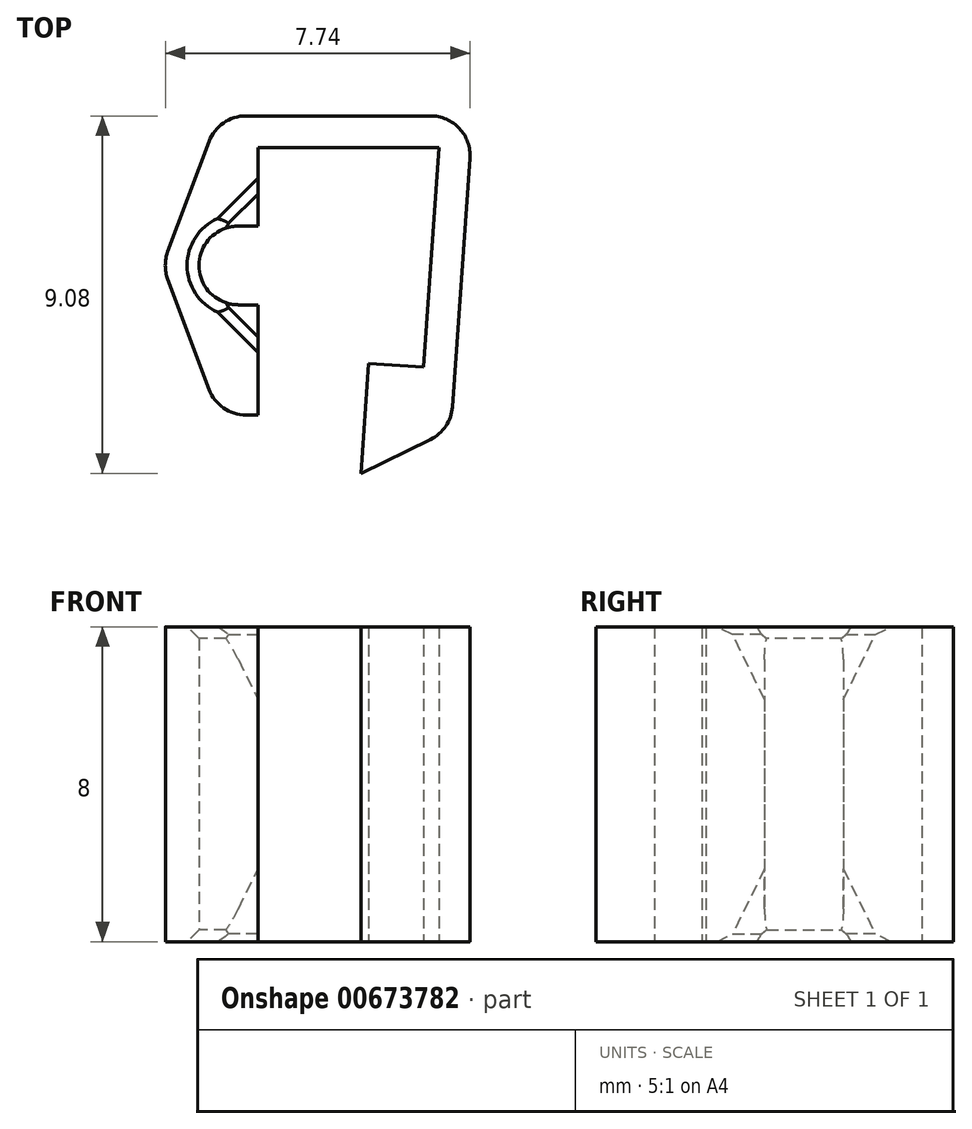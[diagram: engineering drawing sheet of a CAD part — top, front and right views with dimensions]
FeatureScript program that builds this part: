
annotation { "Feature Type Name" : "Feature", "Feature Type Description" : "" }
export const myFeature = defineFeature(function(context is Context, id is Id, definition is map)
    precondition{}
    {
        {
            var Q0;
            Q0=qCreatedBy(makeId("Top.planeOp"),FACE);
            var sketch = newSketch(context, id + "F0", { "sketchPlane" : qUnion([Q0])});
            skLineSegment(sketch, "E0", {"start": v(0, 0) * mm, "end": v(-0.4, -5.59) * mm});
            skLineSegment(sketch, "E1", {"start": v(-0.4, -5.59) * mm, "end": v(-1.79, -5.49) * mm});
            skLineSegment(sketch, "E2", {"start": v(-1.79, -5.49) * mm, "end": v(-1.98, -8.28) * mm});
            skLineSegment(sketch, "E3", {"start": v(-1.98, -8.28) * mm, "end": v(0.3, -7.17) * mm});
            skLineSegment(sketch, "E4", {"start": v(0.3, -7.17) * mm, "end": v(0.86, 0.8) * mm});
            skLineSegment(sketch, "E5", {"start": v(0.86, 0.8) * mm, "end": v(-5.6, 0.8) * mm});
            skLineSegment(sketch, "E6", {"start": v(-5.1, -4) * mm, "end": v(-4.6, -4) * mm});
            skLineSegment(sketch, "E7", {"start": v(-4.6, -4) * mm, "end": v(-4.6, -6.8) * mm});
            skLineSegment(sketch, "E8", {"start": v(-7.02, -3) * mm, "end": v(-5.6, -6.8) * mm});
            skLineSegment(sketch, "E9", {"start": v(-5.6, -6.8) * mm, "end": v(-4.6, -6.8) * mm});
            skLineSegment(sketch, "E10", {"start": v(-4.6, -2) * mm, "end": v(-5.1, -2) * mm});
            skLineSegment(sketch, "E11", {"start": v(0, 0) * mm, "end": v(-4.6, 0) * mm});
            skLineSegment(sketch, "E12", {"start": v(-4.6, 0) * mm, "end": v(-4.6, -2) * mm});
            skArc(sketch, "E13", {"start": v(-5.1, -2) * mm, "mid": v(-6.1, -3) * mm, "end": v(-5.1, -4) * mm});
            skLineSegment(sketch, "E14", {"start": v(-7.02, -3) * mm, "end": v(-5.6, 0.8) * mm});
            skLineSegment(sketch, "E15", {"start": v(-5.6, -6.8) * mm, "end": v(-5.6, 0.8) * mm, "construction": true});
            skLineSegment(sketch, "E16", {"start": v(-5.1, -3) * mm, "end": v(-6.04, -2.65) * mm, "construction": true});
            skLineSegment(sketch, "E17", {"start": v(-6.04, -2.65) * mm, "end": v(-6.79, -2.37) * mm, "construction": true});
            skLineSegment(sketch, "E18", {"start": v(0, 0) * mm, "end": v(0, 0.8) * mm, "construction": true});
            skLineSegment(sketch, "E19", {"start": v(0.8, -0.06) * mm, "end": v(0, 0) * mm, "construction": true});
            skSolve(sketch);
        }
        {
            var Q0;
            Q0=qSketchRegion(id+"F0",true);
            extrude(context, id + "F1", {"entities" : qUnion([Q0]), "depth" : 4 * mm, "offsetDistance" : 25 * mm});
        }
        {
            var Q0;
            Q0=makeQuery(id+"F1.opExtrude","CAP_FACE",FACE,{"disambiguationData":[OSD([sQuery(id+"F0.wireOp",EDGE,"E0"),sQuery(id+"F0.wireOp",EDGE,"E1"),sQuery(id+"F0.wireOp",EDGE,"E2"),sQuery(id+"F0.wireOp",EDGE,"E3"),sQuery(id+"F0.wireOp",EDGE,"E4"),sQuery(id+"F0.wireOp",EDGE,"E5"),sQuery(id+"F0.wireOp",EDGE,"3qQk4eZ2-qFBK-7vCE-47k8-9gwiF50xY8QG"),sQuery(id+"F0.wireOp",EDGE,"FwfflrWr-MbD4-lGZ7-AJjG-6BkzjliF19me"),sQuery(id+"F0.wireOp",EDGE,"E6"),sQuery(id+"F0.wireOp",EDGE,"E7"),sQuery(id+"F0.wireOp",EDGE,"dEJFUDGW-VdPt-nXIw-TINV-OlQtnsbTHH9Y"),sQuery(id+"F0.wireOp",EDGE,"E8"),sQuery(id+"F0.wireOp",EDGE,"E9")])],"isStart":false});
            var sketch = newSketch(context, id + "F2", { "sketchPlane" : qUnion([Q0])});
            skLineSegment(sketch, "E20", {"start": v(-5.8, -3.7) * mm, "end": v(-4.6, -4.91) * mm});
            skLineSegment(sketch, "E21", {"start": v(-4.6, -4.91) * mm, "end": v(-4.6, -4) * mm});
            skLineSegment(sketch, "E22", {"start": v(-4.6, -4) * mm, "end": v(-5.8, -3.7) * mm});
            skLineSegment(sketch, "E23", {"start": v(-5.8, -2.3) * mm, "end": v(-4.6, -1.09) * mm});
            skLineSegment(sketch, "E24", {"start": v(-4.6, -1.09) * mm, "end": v(-4.6, -2) * mm});
            skLineSegment(sketch, "E25", {"start": v(-4.6, -2) * mm, "end": v(-5.8, -2.3) * mm});
            skSolve(sketch);
        }
        {
            var Q0;
            Q0=qSketchRegion(id+"F2",true);
            extrude(context, id + "F3", {"entities" : qUnion([Q0]), "operationType" : NewBodyOperationType.REMOVE, "oppositeDirection" : true, "depth" : 2 * mm});
        }
        {
            var Q0;
            Q0=makeQuery(id+"F3.boolean.opBoolean","COPY",EDGE,{"derivedFrom":makeQuery(id+"F3.opExtrude","CAP_EDGE",EDGE,{"disambiguationData":[OSD([sQuery(id+"F2.wireOp",EDGE,"E20")])],"isStart":false})});
            chamfer(context, id + "F4", {"entities" : qUnion([Q0]), "chamferType" : ChamferType.TWO_OFFSETS, "width1" : .7 * mm, "oppositeDirection" : false, "width2" : 2 * mm, "tangentPropagation" : true});
        }
        {
            var Q0;
            Q0=makeQuery(id+"F3.boolean.opBoolean","COPY",EDGE,{"derivedFrom":makeQuery(id+"F3.opExtrude","CAP_EDGE",EDGE,{"disambiguationData":[OSD([sQuery(id+"F2.wireOp",EDGE,"E23")])],"isStart":false})});
            chamfer(context, id + "F5", {"entities" : qUnion([Q0]), "chamferType" : ChamferType.TWO_OFFSETS, "width1" : 2 * mm, "oppositeDirection" : false, "width2" : .7 * mm, "tangentPropagation" : true});
        }
        {
            var Q0;
            Q0=makeQuery(id+"F1.opExtrude","SWEPT_EDGE",EDGE,{"disambiguationData":[OSD([sQuery(id+"F0.wireOp",EDGE,"E4"),sQuery(id+"F0.wireOp",EDGE,"E5")])]});
            var Q1;
            Q1=makeQuery(id+"F1.opExtrude","SWEPT_EDGE",EDGE,{"disambiguationData":[OSD([sQuery(id+"F0.wireOp",EDGE,"E3"),sQuery(id+"F0.wireOp",EDGE,"E4")])]});
            var Q2;
            Q2=makeQuery(id+"F1.opExtrude","SWEPT_EDGE",EDGE,{"disambiguationData":[OSD([sQuery(id+"F0.wireOp",EDGE,"E8"),sQuery(id+"F0.wireOp",EDGE,"E9")])]});
            var Q3;
            Q3=makeQuery(id+"F1.opExtrude","SWEPT_EDGE",EDGE,{"disambiguationData":[OSD([sQuery(id+"F0.wireOp",EDGE,"E8"),sQuery(id+"F0.wireOp",EDGE,"E14")])]});
            var Q4;
            Q4=makeQuery(id+"F1.opExtrude","SWEPT_EDGE",EDGE,{"disambiguationData":[OSD([sQuery(id+"F0.wireOp",EDGE,"E5"),sQuery(id+"F0.wireOp",EDGE,"E14")])]});
            fillet(context, id + "F6", {"entities" : qUnion([Q0, Q1, Q2, Q3, Q4]), "radius" : 1 * mm, "tangentPropagation" : true, "allowEdgeOverflow" : false});
        }
        {
            var Q0;
            Q0=makeQuery(id+"F1.opExtrude","SWEPT_BODY",BODY,{"disambiguationData":[OSD([sQuery(id+"F0.wireOp",EDGE,"E0"),sQuery(id+"F0.wireOp",EDGE,"E1"),sQuery(id+"F0.wireOp",EDGE,"E2"),sQuery(id+"F0.wireOp",EDGE,"E3"),sQuery(id+"F0.wireOp",EDGE,"E4"),sQuery(id+"F0.wireOp",EDGE,"E5"),sQuery(id+"F0.wireOp",EDGE,"3qQk4eZ2-qFBK-7vCE-47k8-9gwiF50xY8QG"),sQuery(id+"F0.wireOp",EDGE,"FwfflrWr-MbD4-lGZ7-AJjG-6BkzjliF19me"),sQuery(id+"F0.wireOp",EDGE,"E6"),sQuery(id+"F0.wireOp",EDGE,"E7"),sQuery(id+"F0.wireOp",EDGE,"dEJFUDGW-VdPt-nXIw-TINV-OlQtnsbTHH9Y"),sQuery(id+"F0.wireOp",EDGE,"E8"),sQuery(id+"F0.wireOp",EDGE,"E9")])]});
            var Q1;
            Q1=makeQuery(id+"F1.opExtrude","CAP_FACE",FACE,{"disambiguationData":[OSD([sQuery(id+"F0.wireOp",EDGE,"E0"),sQuery(id+"F0.wireOp",EDGE,"E1"),sQuery(id+"F0.wireOp",EDGE,"E2"),sQuery(id+"F0.wireOp",EDGE,"E3"),sQuery(id+"F0.wireOp",EDGE,"E4"),sQuery(id+"F0.wireOp",EDGE,"E5"),sQuery(id+"F0.wireOp",EDGE,"3qQk4eZ2-qFBK-7vCE-47k8-9gwiF50xY8QG"),sQuery(id+"F0.wireOp",EDGE,"FwfflrWr-MbD4-lGZ7-AJjG-6BkzjliF19me"),sQuery(id+"F0.wireOp",EDGE,"E6"),sQuery(id+"F0.wireOp",EDGE,"E7"),sQuery(id+"F0.wireOp",EDGE,"dEJFUDGW-VdPt-nXIw-TINV-OlQtnsbTHH9Y"),sQuery(id+"F0.wireOp",EDGE,"E8"),sQuery(id+"F0.wireOp",EDGE,"E9")])],"isStart":true});
            mirror(context, id + "F7", {"operationType" : NewBodyOperationType.ADD, "entities" : qUnion([Q0]), "mirrorPlane" : qUnion([Q1])});
        }
        {
            var Q0;
            Q0=makeQuery(id+"F1.opExtrude","CAP_EDGE",EDGE,{"disambiguationData":[OSD([sQuery(id+"F0.wireOp",EDGE,"E13")])],"isStart":false});
            var Q1;
            Q1=makeQuery(id+"F5.opChamfer","BLEND_EDGE",EDGE,{"blendedFrom":[makeQuery(id+"F3.boolean.opBoolean","COPY",EDGE,{"derivedFrom":makeQuery(id+"F3.opExtrude","CAP_EDGE",EDGE,{"disambiguationData":[OSD([sQuery(id+"F2.wireOp",EDGE,"E23")])],"isStart":false})}),makeQuery(id+"F1.opExtrude","CAP_FACE",FACE,{"disambiguationData":[OSD([sQuery(id+"F0.wireOp",EDGE,"E0"),sQuery(id+"F0.wireOp",EDGE,"E1"),sQuery(id+"F0.wireOp",EDGE,"E2"),sQuery(id+"F0.wireOp",EDGE,"E3"),sQuery(id+"F0.wireOp",EDGE,"E4"),sQuery(id+"F0.wireOp",EDGE,"E5"),sQuery(id+"F0.wireOp",EDGE,"E6"),sQuery(id+"F0.wireOp",EDGE,"E7"),sQuery(id+"F0.wireOp",EDGE,"E8"),sQuery(id+"F0.wireOp",EDGE,"E9"),sQuery(id+"F0.wireOp",EDGE,"E10"),sQuery(id+"F0.wireOp",EDGE,"E11"),sQuery(id+"F0.wireOp",EDGE,"E12"),sQuery(id+"F0.wireOp",EDGE,"E13"),sQuery(id+"F0.wireOp",EDGE,"E14")])],"isStart":false})],"blendedInto":[makeQuery(id+"F1.opExtrude","CAP_FACE",FACE,{"disambiguationData":[OSD([sQuery(id+"F0.wireOp",EDGE,"E0"),sQuery(id+"F0.wireOp",EDGE,"E1"),sQuery(id+"F0.wireOp",EDGE,"E2"),sQuery(id+"F0.wireOp",EDGE,"E3"),sQuery(id+"F0.wireOp",EDGE,"E4"),sQuery(id+"F0.wireOp",EDGE,"E5"),sQuery(id+"F0.wireOp",EDGE,"E6"),sQuery(id+"F0.wireOp",EDGE,"E7"),sQuery(id+"F0.wireOp",EDGE,"E8"),sQuery(id+"F0.wireOp",EDGE,"E9"),sQuery(id+"F0.wireOp",EDGE,"E10"),sQuery(id+"F0.wireOp",EDGE,"E11"),sQuery(id+"F0.wireOp",EDGE,"E12"),sQuery(id+"F0.wireOp",EDGE,"E13"),sQuery(id+"F0.wireOp",EDGE,"E14")])],"isStart":false})]});
            var Q2;
            Q2=makeQuery(id+"F4.opChamfer","BLEND_EDGE",EDGE,{"blendedFrom":[makeQuery(id+"F3.boolean.opBoolean","COPY",EDGE,{"derivedFrom":makeQuery(id+"F3.opExtrude","CAP_EDGE",EDGE,{"disambiguationData":[OSD([sQuery(id+"F2.wireOp",EDGE,"E20")])],"isStart":false})}),makeQuery(id+"F1.opExtrude","CAP_FACE",FACE,{"disambiguationData":[OSD([sQuery(id+"F0.wireOp",EDGE,"E0"),sQuery(id+"F0.wireOp",EDGE,"E1"),sQuery(id+"F0.wireOp",EDGE,"E2"),sQuery(id+"F0.wireOp",EDGE,"E3"),sQuery(id+"F0.wireOp",EDGE,"E4"),sQuery(id+"F0.wireOp",EDGE,"E5"),sQuery(id+"F0.wireOp",EDGE,"E6"),sQuery(id+"F0.wireOp",EDGE,"E7"),sQuery(id+"F0.wireOp",EDGE,"E8"),sQuery(id+"F0.wireOp",EDGE,"E9"),sQuery(id+"F0.wireOp",EDGE,"E10"),sQuery(id+"F0.wireOp",EDGE,"E11"),sQuery(id+"F0.wireOp",EDGE,"E12"),sQuery(id+"F0.wireOp",EDGE,"E13"),sQuery(id+"F0.wireOp",EDGE,"E14")])],"isStart":false})],"blendedInto":[makeQuery(id+"F1.opExtrude","CAP_FACE",FACE,{"disambiguationData":[OSD([sQuery(id+"F0.wireOp",EDGE,"E0"),sQuery(id+"F0.wireOp",EDGE,"E1"),sQuery(id+"F0.wireOp",EDGE,"E2"),sQuery(id+"F0.wireOp",EDGE,"E3"),sQuery(id+"F0.wireOp",EDGE,"E4"),sQuery(id+"F0.wireOp",EDGE,"E5"),sQuery(id+"F0.wireOp",EDGE,"E6"),sQuery(id+"F0.wireOp",EDGE,"E7"),sQuery(id+"F0.wireOp",EDGE,"E8"),sQuery(id+"F0.wireOp",EDGE,"E9"),sQuery(id+"F0.wireOp",EDGE,"E10"),sQuery(id+"F0.wireOp",EDGE,"E11"),sQuery(id+"F0.wireOp",EDGE,"E12"),sQuery(id+"F0.wireOp",EDGE,"E13"),sQuery(id+"F0.wireOp",EDGE,"E14")])],"isStart":false})]});
            var Q3;
            Q3=makeQuery(id+"F7.opPattern","COPY",EDGE,{"derivedFrom":makeQuery(id+"F1.opExtrude","CAP_EDGE",EDGE,{"disambiguationData":[OSD([sQuery(id+"F0.wireOp",EDGE,"E13")])],"isStart":false}),"instanceName":"1"});
            var Q4;
            Q4=makeQuery(id+"F7.opPattern","COPY",EDGE,{"derivedFrom":makeQuery(id+"F5.opChamfer","BLEND_EDGE",EDGE,{"blendedFrom":[makeQuery(id+"F3.boolean.opBoolean","COPY",EDGE,{"derivedFrom":makeQuery(id+"F3.opExtrude","CAP_EDGE",EDGE,{"disambiguationData":[OSD([sQuery(id+"F2.wireOp",EDGE,"E23")])],"isStart":false})}),makeQuery(id+"F1.opExtrude","CAP_FACE",FACE,{"disambiguationData":[OSD([sQuery(id+"F0.wireOp",EDGE,"E0"),sQuery(id+"F0.wireOp",EDGE,"E1"),sQuery(id+"F0.wireOp",EDGE,"E2"),sQuery(id+"F0.wireOp",EDGE,"E3"),sQuery(id+"F0.wireOp",EDGE,"E4"),sQuery(id+"F0.wireOp",EDGE,"E5"),sQuery(id+"F0.wireOp",EDGE,"E6"),sQuery(id+"F0.wireOp",EDGE,"E7"),sQuery(id+"F0.wireOp",EDGE,"E8"),sQuery(id+"F0.wireOp",EDGE,"E9"),sQuery(id+"F0.wireOp",EDGE,"E10"),sQuery(id+"F0.wireOp",EDGE,"E11"),sQuery(id+"F0.wireOp",EDGE,"E12"),sQuery(id+"F0.wireOp",EDGE,"E13"),sQuery(id+"F0.wireOp",EDGE,"E14")])],"isStart":false})],"blendedInto":[makeQuery(id+"F1.opExtrude","CAP_FACE",FACE,{"disambiguationData":[OSD([sQuery(id+"F0.wireOp",EDGE,"E0"),sQuery(id+"F0.wireOp",EDGE,"E1"),sQuery(id+"F0.wireOp",EDGE,"E2"),sQuery(id+"F0.wireOp",EDGE,"E3"),sQuery(id+"F0.wireOp",EDGE,"E4"),sQuery(id+"F0.wireOp",EDGE,"E5"),sQuery(id+"F0.wireOp",EDGE,"E6"),sQuery(id+"F0.wireOp",EDGE,"E7"),sQuery(id+"F0.wireOp",EDGE,"E8"),sQuery(id+"F0.wireOp",EDGE,"E9"),sQuery(id+"F0.wireOp",EDGE,"E10"),sQuery(id+"F0.wireOp",EDGE,"E11"),sQuery(id+"F0.wireOp",EDGE,"E12"),sQuery(id+"F0.wireOp",EDGE,"E13"),sQuery(id+"F0.wireOp",EDGE,"E14")])],"isStart":false})]}),"instanceName":"1"});
            var Q5;
            Q5=makeQuery(id+"F7.opPattern","COPY",EDGE,{"derivedFrom":makeQuery(id+"F4.opChamfer","BLEND_EDGE",EDGE,{"blendedFrom":[makeQuery(id+"F3.boolean.opBoolean","COPY",EDGE,{"derivedFrom":makeQuery(id+"F3.opExtrude","CAP_EDGE",EDGE,{"disambiguationData":[OSD([sQuery(id+"F2.wireOp",EDGE,"E20")])],"isStart":false})}),makeQuery(id+"F1.opExtrude","CAP_FACE",FACE,{"disambiguationData":[OSD([sQuery(id+"F0.wireOp",EDGE,"E0"),sQuery(id+"F0.wireOp",EDGE,"E1"),sQuery(id+"F0.wireOp",EDGE,"E2"),sQuery(id+"F0.wireOp",EDGE,"E3"),sQuery(id+"F0.wireOp",EDGE,"E4"),sQuery(id+"F0.wireOp",EDGE,"E5"),sQuery(id+"F0.wireOp",EDGE,"E6"),sQuery(id+"F0.wireOp",EDGE,"E7"),sQuery(id+"F0.wireOp",EDGE,"E8"),sQuery(id+"F0.wireOp",EDGE,"E9"),sQuery(id+"F0.wireOp",EDGE,"E10"),sQuery(id+"F0.wireOp",EDGE,"E11"),sQuery(id+"F0.wireOp",EDGE,"E12"),sQuery(id+"F0.wireOp",EDGE,"E13"),sQuery(id+"F0.wireOp",EDGE,"E14")])],"isStart":false})],"blendedInto":[makeQuery(id+"F1.opExtrude","CAP_FACE",FACE,{"disambiguationData":[OSD([sQuery(id+"F0.wireOp",EDGE,"E0"),sQuery(id+"F0.wireOp",EDGE,"E1"),sQuery(id+"F0.wireOp",EDGE,"E2"),sQuery(id+"F0.wireOp",EDGE,"E3"),sQuery(id+"F0.wireOp",EDGE,"E4"),sQuery(id+"F0.wireOp",EDGE,"E5"),sQuery(id+"F0.wireOp",EDGE,"E6"),sQuery(id+"F0.wireOp",EDGE,"E7"),sQuery(id+"F0.wireOp",EDGE,"E8"),sQuery(id+"F0.wireOp",EDGE,"E9"),sQuery(id+"F0.wireOp",EDGE,"E10"),sQuery(id+"F0.wireOp",EDGE,"E11"),sQuery(id+"F0.wireOp",EDGE,"E12"),sQuery(id+"F0.wireOp",EDGE,"E13"),sQuery(id+"F0.wireOp",EDGE,"E14")])],"isStart":false})]}),"instanceName":"1"});
            chamfer(context, id + "F8", {"entities" : qUnion([Q0, Q1, Q2, Q3, Q4, Q5]), "chamferType" : ChamferType.OFFSET_ANGLE, "width" : .3 * mm, "oppositeDirection" : false, "angle" : 45 * degree, "tangentPropagation" : true});
        }
    });
